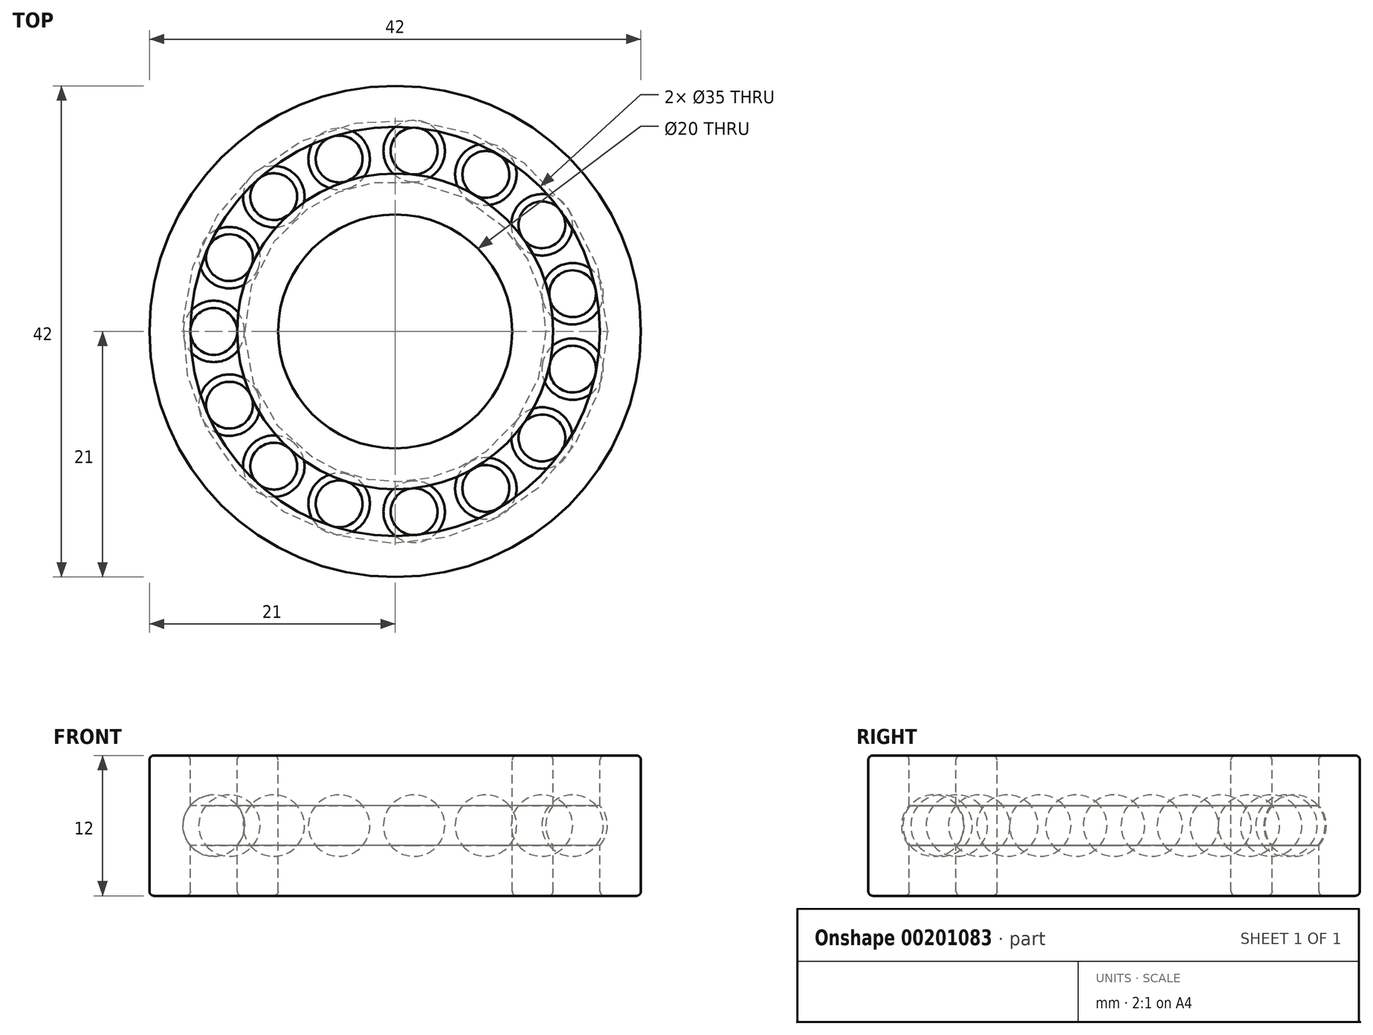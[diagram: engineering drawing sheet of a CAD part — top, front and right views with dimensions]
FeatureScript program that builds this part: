
annotation { "Feature Type Name" : "Feature", "Feature Type Description" : "" }
export const myFeature = defineFeature(function(context is Context, id is Id, definition is map)
    precondition{}
    {
        {
            var Q0;
            Q0=qCreatedBy(makeId("Front.planeOp"),FACE);
            var sketch = newSketch(context, id + "F0", { "sketchPlane" : qUnion([Q0])});
            skLineSegment(sketch, "E0.right", {"start": v(-21, 5.6) * mm, "end": v(-21, -5.6) * mm});
            skPoint(sketch, "E0.middle", {"position": v(0, 0) * mm});
            skLineSegment(sketch, "E1.right", {"start": v(-10, 5.6) * mm, "end": v(-10, -5.6) * mm});
            skArc(sketch, "E2", {"start": v(-17.5, 1.7) * mm, "mid": v(-18.12, 0) * mm, "end": v(-17.5, -1.7) * mm});
            skPoint(sketch, "E2.centerSnap0", {"position": v(-21, 0) * mm});
            skLineSegment(sketch, "E3", {"start": v(-21, 0) * mm, "end": v(-10, 0) * mm, "construction": true});
            skLineSegment(sketch, "E4.left", {"start": v(-13.5, 5.6) * mm, "end": v(-13.5, 1.7) * mm});
            skLineSegment(sketch, "E4.right", {"start": v(-17.5, 5.6) * mm, "end": v(-17.5, 1.7) * mm});
            skLineSegment(sketch, "E5.trimOffspring", {"start": v(-17.5, -1.7) * mm, "end": v(-17.5, -5.6) * mm});
            skArc(sketch, "E6.trimOffspring", {"start": v(-13.5, -1.7) * mm, "mid": v(-12.87, 0) * mm, "end": v(-13.5, 1.7) * mm});
            skLineSegment(sketch, "E7.trimOffspring", {"start": v(-17.9, 6) * mm, "end": v(-20.6, 6) * mm});
            skLineSegment(sketch, "E8.trimOffspring", {"start": v(-10.4, 6) * mm, "end": v(-13.1, 6) * mm});
            skLineSegment(sketch, "E9.trimOffspring", {"start": v(-10.4, -6) * mm, "end": v(-13.1, -6) * mm});
            skPoint(sketch, "E0.top.end.orphan", {"position": v(10, -6) * mm});
            skPoint(sketch, "E0.left.end.orphan", {"position": v(21, -6) * mm});
            skPoint(sketch, "E0.bottom.end.orphan", {"position": v(10, 6) * mm});
            skPoint(sketch, "E0.bottom.start.orphan", {"position": v(21, 6) * mm});
            skLineSegment(sketch, "E10.trimOffspring", {"start": v(-17.9, -6) * mm, "end": v(-20.6, -6) * mm});
            skLineSegment(sketch, "E11.trimOffspring", {"start": v(-13.5, -1.7) * mm, "end": v(-13.5, -5.6) * mm});
            skPoint(sketch, "E12.visualSharp", {"position": v(-21, 6) * mm});
            skArc(sketch, "E12.filletArc", {"start": v(-20.6, 6) * mm, "mid": v(-20.88, 5.88) * mm, "end": v(-21, 5.6) * mm});
            skPoint(sketch, "E13.visualSharp", {"position": v(-21, -6) * mm});
            skArc(sketch, "E13.filletArc", {"start": v(-21, -5.6) * mm, "mid": v(-20.88, -5.88) * mm, "end": v(-20.6, -6) * mm});
            skPoint(sketch, "E14.visualSharp", {"position": v(-17.5, -6) * mm});
            skArc(sketch, "E14.filletArc", {"start": v(-17.9, -6) * mm, "mid": v(-17.62, -5.88) * mm, "end": v(-17.5, -5.6) * mm});
            skPoint(sketch, "E15.visualSharp", {"position": v(-13.5, -6) * mm});
            skArc(sketch, "E15.filletArc", {"start": v(-13.5, -5.6) * mm, "mid": v(-13.38, -5.88) * mm, "end": v(-13.1, -6) * mm});
            skPoint(sketch, "E16.visualSharp", {"position": v(-10, -6) * mm});
            skArc(sketch, "E16.filletArc", {"start": v(-10.4, -6) * mm, "mid": v(-10.12, -5.88) * mm, "end": v(-10, -5.6) * mm});
            skPoint(sketch, "E17.visualSharp", {"position": v(-10, 6) * mm});
            skArc(sketch, "E17.filletArc", {"start": v(-10, 5.6) * mm, "mid": v(-10.12, 5.88) * mm, "end": v(-10.4, 6) * mm});
            skPoint(sketch, "E18.visualSharp", {"position": v(-13.5, 6) * mm});
            skArc(sketch, "E18.filletArc", {"start": v(-13.1, 6) * mm, "mid": v(-13.38, 5.88) * mm, "end": v(-13.5, 5.6) * mm});
            skPoint(sketch, "E19.visualSharp", {"position": v(-17.5, 6) * mm});
            skArc(sketch, "E19.filletArc", {"start": v(-17.5, 5.6) * mm, "mid": v(-17.62, 5.88) * mm, "end": v(-17.9, 6) * mm});
            skLineSegment(sketch, "E20", {"start": v(0, 23.97) * mm, "end": v(0, -23.97) * mm});
            skCircle(sketch, "E21", {"center": v(-15.5, 0) * mm, "radius": 2.63 * mm});
            skLineSegment(sketch, "E22", {"start": v(-15.5, 2.63) * mm, "end": v(-15.5, -2.63) * mm});
            skSolve(sketch);
        }
        {
            var Q0;
            Q0=makeQuery(id+"F0.imprint","IMPRINT",FACE,{"disambiguationData":[TD([[makeQuery(id+"F0.imprint","IMPRINT",EDGE,{"derivedFrom":sQuery(id+"F0.wireOp",EDGE,"E1.right")}),-1.0]])]});
            var Q1;
            Q1=sQuery(id+"F0.wireOp",EDGE,"E20");
            revolve(context, id + "F1", {"entities" : qUnion([Q0]), "axis" : qUnion([Q1]), "revolveType" : RevolveType.FULL});
        }
        {
            var Q0;
            {var subQ0=sQuery(id+"F0.wireOp",EDGE,"E22");Q0=makeQuery(id+"F0.imprint","IMPRINT",FACE,{"disambiguationData":[TD([[makeQuery(id+"F0.imprint","IMPRINT",EDGE,{"derivedFrom":subQ0}),-1.0]])]});}
            var Q1;
            Q1=sQuery(id+"F0.wireOp",EDGE,"E22");
            revolve(context, id + "F2", {"operationType" : NewBodyOperationType.ADD, "entities" : qUnion([Q0]), "axis" : qUnion([Q1]), "revolveType" : RevolveType.FULL});
        }
        {
            var Q0;
            Q0=makeQuery(id+"F0.imprint","IMPRINT",FACE,{"disambiguationData":[TD([[makeQuery(id+"F0.imprint","IMPRINT",EDGE,{"derivedFrom":sQuery(id+"F0.wireOp",EDGE,"E0.right")}),1.0]])]});
            var Q1;
            Q1=sQuery(id+"F0.wireOp",EDGE,"E20");
            revolve(context, id + "F3", {"entities" : qUnion([Q0]), "axis" : qUnion([Q1]), "revolveType" : RevolveType.FULL});
        }
        {
            var Q0;
            Q0=makeQuery(id+"F2.opRevolve","SWEPT_BODY",BODY,{"disambiguationData":[OSD([sQuery(id+"F0.wireOp",EDGE,"E21"),sQuery(id+"F0.wireOp",EDGE,"E22")])]});
            var Q1;
            Q1=sQuery(id+"F0.wireOp",EDGE,"E20");
            circularPattern(context, id + "F4", {"entities" : qUnion([Q0]), "axis" : qUnion([Q1]), "angle" : 360 * degree, "instanceCount" : 15, "equalSpace" : true});
        }
    });
